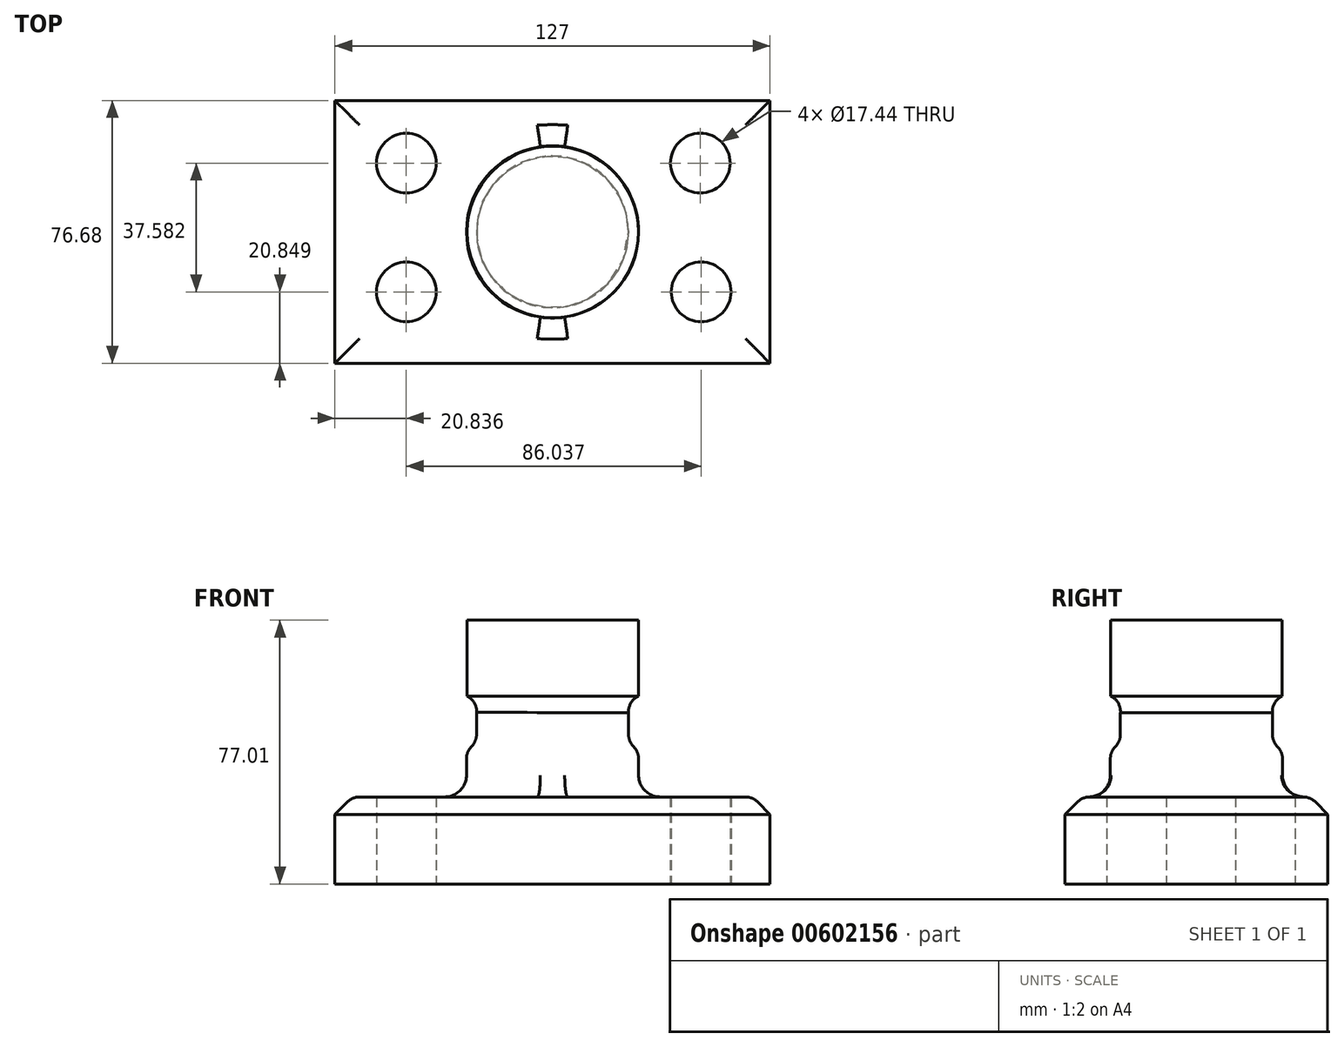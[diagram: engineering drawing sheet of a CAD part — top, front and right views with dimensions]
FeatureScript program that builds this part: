
annotation { "Feature Type Name" : "Feature", "Feature Type Description" : "" }
export const myFeature = defineFeature(function(context is Context, id is Id, definition is map)
    precondition{}
    {
        {
            var Q0;
            Q0=qCreatedBy(makeId("Top.planeOp"),FACE);
            var sketch = newSketch(context, id + "F0", { "sketchPlane" : qUnion([Q0])});
            skLineSegment(sketch, "E0.bottom", {"start": v(63.5, -38.34) * mm, "end": v(-63.5, -38.34) * mm});
            skLineSegment(sketch, "E0.top", {"start": v(63.5, 38.34) * mm, "end": v(-63.5, 38.34) * mm});
            skLineSegment(sketch, "E0.left", {"start": v(63.5, -38.34) * mm, "end": v(63.5, 38.34) * mm});
            skLineSegment(sketch, "E0.right", {"start": v(-63.5, -38.34) * mm, "end": v(-63.5, 38.34) * mm});
            skPoint(sketch, "E0.middle", {"position": v(0, 0) * mm});
            skSolve(sketch);
        }
        {
            var Q0;
            Q0=makeQuery(id+"F0.imprint","IMPRINT",FACE,{"disambiguationData":[TD([[makeQuery(id+"F0.imprint","IMPRINT",EDGE,{"derivedFrom":sQuery(id+"F0.wireOp",EDGE,"E0.bottom")}),-1.0]])]});
            var Q1;
            Q1=sQuery(id+"F0.wireOp",EDGE,"E0.bottom");
            var Q2;
            Q2=sQuery(id+"F0.wireOp",EDGE,"E0.top");
            extrude(context, id + "F1", {"entities" : qUnion([Q0]), "surfaceEntities" : qUnion([Q1, Q2]), "depth" : 25.4 * mm, "offsetDistance" : 25.4 * mm});
        }
        {
            var Q0;
            Q0=makeQuery(id+"F1.opExtrude","CAP_EDGE",EDGE,{"disambiguationData":[OSD([sQuery(id+"F0.wireOp",EDGE,"E0.bottom")])],"isStart":false});
            var Q1;
            Q1=makeQuery(id+"F1.opExtrude","CAP_EDGE",EDGE,{"disambiguationData":[OSD([sQuery(id+"F0.wireOp",EDGE,"E0.right")])],"isStart":false});
            var Q2;
            Q2=makeQuery(id+"F1.opExtrude","CAP_FACE",FACE,{"disambiguationData":[OSD([sQuery(id+"F0.wireOp",EDGE,"E0.bottom"),sQuery(id+"F0.wireOp",EDGE,"E0.top"),sQuery(id+"F0.wireOp",EDGE,"E0.left"),sQuery(id+"F0.wireOp",EDGE,"E0.right")])],"isStart":false});
            chamfer(context, id + "F2", {"entities" : qUnion([Q0, Q1, Q2]), "width" : 5.08 * mm, "tangentPropagation" : true});
        }
        {
            var Q0;
            Q0=qCreatedBy(makeId("Top.planeOp"),FACE);
            var sketch = newSketch(context, id + "F3", { "sketchPlane" : qUnion([Q0])});
            skCircle(sketch, "E1", {"center": v(-42.66, 20.1) * mm, "radius": 8.72 * mm});
            skCircle(sketch, "E2", {"center": v(-42.66, -17.5) * mm, "radius": 8.72 * mm});
            skCircle(sketch, "E3", {"center": v(43.37, -17.5) * mm, "radius": 8.72 * mm});
            skCircle(sketch, "E4", {"center": v(43.14, 20.1) * mm, "radius": 8.72 * mm});
            skSolve(sketch);
        }
        {
            var Q0;
            Q0=makeQuery(id+"F3.imprint","IMPRINT",FACE,{"disambiguationData":[TD([[makeQuery(id+"F3.imprint","IMPRINT",EDGE,{"derivedFrom":sQuery(id+"F3.wireOp",EDGE,"E2")}),1.0]])]});
            var Q1;
            Q1=makeQuery(id+"F3.imprint","IMPRINT",FACE,{"disambiguationData":[TD([[makeQuery(id+"F3.imprint","IMPRINT",EDGE,{"derivedFrom":sQuery(id+"F3.wireOp",EDGE,"E1")}),1.0]])]});
            var Q2;
            Q2=makeQuery(id+"F3.imprint","IMPRINT",FACE,{"disambiguationData":[TD([[makeQuery(id+"F3.imprint","IMPRINT",EDGE,{"derivedFrom":sQuery(id+"F3.wireOp",EDGE,"E4")}),1.0]])]});
            var Q3;
            Q3=makeQuery(id+"F3.imprint","IMPRINT",FACE,{"disambiguationData":[TD([[makeQuery(id+"F3.imprint","IMPRINT",EDGE,{"derivedFrom":sQuery(id+"F3.wireOp",EDGE,"E3")}),1.0]])]});
            extrude(context, id + "F4", {"entities" : qUnion([Q0, Q1, Q2, Q3]), "operationType" : NewBodyOperationType.REMOVE, "depth" : 54.6 * mm, "offsetDistance" : 25.4 * mm});
        }
        {
            var Q0;
            Q0=qCreatedBy(makeId("Top.planeOp"),FACE);
            var sketch = newSketch(context, id + "F5", { "sketchPlane" : qUnion([Q0])});
            skCircle(sketch, "E5", {"center": v(0, 0) * mm, "radius": 25.12 * mm});
            skCircle(sketch, "E6", {"center": v(0, 0) * mm, "radius": 22.18 * mm});
            skSolve(sketch);
        }
        {
            var Q0;
            Q0=makeQuery(id+"F5.imprint","IMPRINT",FACE,{"disambiguationData":[TD([[makeQuery(id+"F5.imprint","IMPRINT",EDGE,{"derivedFrom":sQuery(id+"F5.wireOp",EDGE,"E5")}),1.0]])]});
            extrude(context, id + "F6", {"entities" : qUnion([Q0]), "operationType" : NewBodyOperationType.ADD, "depth" : 41.15 * mm, "offsetDistance" : 25.4 * mm});
        }
        {
            var Q0;
            Q0=makeQuery(id+"F6.boolean.opBoolean","SPLIT",FACE,{"disambiguationData":[TD([makeQuery(id+"F6.opExtrude","SWEPT_FACE",FACE,{"disambiguationData":[OSD([sQuery(id+"F5.wireOp",EDGE,"E6")])]})])],"derivedFrom":makeQuery(id+"F1.opExtrude","CAP_FACE",FACE,{"disambiguationData":[OSD([sQuery(id+"F0.wireOp",EDGE,"E0.bottom"),sQuery(id+"F0.wireOp",EDGE,"E0.top"),sQuery(id+"F0.wireOp",EDGE,"E0.left"),sQuery(id+"F0.wireOp",EDGE,"E0.right")])],"isStart":false})});
            extrude(context, id + "F7", {"entities" : qUnion([Q0]), "operationType" : NewBodyOperationType.ADD, "depth" : 29.46 * mm, "offsetDistance" : 25.4 * mm});
        }
        {
            var Q0;
            Q0=makeQuery(id+"F6.opExtrude","CAP_EDGE",EDGE,{"disambiguationData":[OSD([sQuery(id+"F5.wireOp",EDGE,"E5")])],"isStart":false});
            var Q1;
            Q1=makeQuery(id+"F7.opExtrude","CAP_EDGE",EDGE,{"disambiguationData":[OSD([sQuery(id+"F0.wireOp",EDGE,"E0.bottom"),sQuery(id+"F0.wireOp",EDGE,"E0.top"),sQuery(id+"F0.wireOp",EDGE,"E0.left"),sQuery(id+"F0.wireOp",EDGE,"E0.right"),sQuery(id+"F5.wireOp",EDGE,"E6")])],"isStart":false});
            fillet(context, id + "F8", {"entities" : qUnion([Q0, Q1]), "radius" : 5.08 * mm, "tangentPropagation" : true, "allowEdgeOverflow" : false});
        }
        {
            var Q0;
            {var subQ0=sQuery(id+"F0.wireOp",EDGE,"E0.bottom");Q0=makeQuery(id+"F2.opChamfer","BLEND_EDGE",EDGE,{"blendedFrom":[makeQuery(id+"F1.opExtrude","CAP_EDGE",EDGE,{"disambiguationData":[OSD([subQ0])],"isStart":false}),makeQuery(id+"F1.opExtrude","CAP_FACE",FACE,{"disambiguationData":[OSD([subQ0,sQuery(id+"F0.wireOp",EDGE,"E0.top"),sQuery(id+"F0.wireOp",EDGE,"E0.left"),sQuery(id+"F0.wireOp",EDGE,"E0.right")])],"isStart":false})],"blendedInto":[makeQuery(id+"F1.opExtrude","CAP_FACE",FACE,{"disambiguationData":[OSD([subQ0,sQuery(id+"F0.wireOp",EDGE,"E0.top"),sQuery(id+"F0.wireOp",EDGE,"E0.left"),sQuery(id+"F0.wireOp",EDGE,"E0.right")])],"isStart":false})]});}
            var Q1;
            {var subQ0=sQuery(id+"F0.wireOp",EDGE,"E0.left");Q1=makeQuery(id+"F2.opChamfer","BLEND_EDGE",EDGE,{"blendedFrom":[makeQuery(id+"F1.opExtrude","CAP_EDGE",EDGE,{"disambiguationData":[OSD([subQ0])],"isStart":false}),makeQuery(id+"F1.opExtrude","CAP_FACE",FACE,{"disambiguationData":[OSD([sQuery(id+"F0.wireOp",EDGE,"E0.bottom"),sQuery(id+"F0.wireOp",EDGE,"E0.top"),subQ0,sQuery(id+"F0.wireOp",EDGE,"E0.right")])],"isStart":false})],"blendedInto":[makeQuery(id+"F1.opExtrude","CAP_FACE",FACE,{"disambiguationData":[OSD([sQuery(id+"F0.wireOp",EDGE,"E0.bottom"),sQuery(id+"F0.wireOp",EDGE,"E0.top"),subQ0,sQuery(id+"F0.wireOp",EDGE,"E0.right")])],"isStart":false})]});}
            var Q2;
            {var subQ0=sQuery(id+"F0.wireOp",EDGE,"E0.right");Q2=makeQuery(id+"F2.opChamfer","BLEND_EDGE",EDGE,{"blendedFrom":[makeQuery(id+"F1.opExtrude","CAP_EDGE",EDGE,{"disambiguationData":[OSD([subQ0])],"isStart":false}),makeQuery(id+"F1.opExtrude","CAP_FACE",FACE,{"disambiguationData":[OSD([sQuery(id+"F0.wireOp",EDGE,"E0.bottom"),sQuery(id+"F0.wireOp",EDGE,"E0.top"),sQuery(id+"F0.wireOp",EDGE,"E0.left"),subQ0])],"isStart":false})],"blendedInto":[makeQuery(id+"F1.opExtrude","CAP_FACE",FACE,{"disambiguationData":[OSD([sQuery(id+"F0.wireOp",EDGE,"E0.bottom"),sQuery(id+"F0.wireOp",EDGE,"E0.top"),sQuery(id+"F0.wireOp",EDGE,"E0.left"),subQ0])],"isStart":false})]});}
            var Q3;
            {var subQ0=sQuery(id+"F0.wireOp",EDGE,"E0.top");Q3=makeQuery(id+"F2.opChamfer","BLEND_EDGE",EDGE,{"blendedFrom":[makeQuery(id+"F1.opExtrude","CAP_EDGE",EDGE,{"disambiguationData":[OSD([subQ0])],"isStart":false}),makeQuery(id+"F1.opExtrude","CAP_FACE",FACE,{"disambiguationData":[OSD([sQuery(id+"F0.wireOp",EDGE,"E0.bottom"),subQ0,sQuery(id+"F0.wireOp",EDGE,"E0.left"),sQuery(id+"F0.wireOp",EDGE,"E0.right")])],"isStart":false})],"blendedInto":[makeQuery(id+"F1.opExtrude","CAP_FACE",FACE,{"disambiguationData":[OSD([sQuery(id+"F0.wireOp",EDGE,"E0.bottom"),subQ0,sQuery(id+"F0.wireOp",EDGE,"E0.left"),sQuery(id+"F0.wireOp",EDGE,"E0.right")])],"isStart":false})]});}
            fillet(context, id + "F9", {"entities" : qUnion([Q0, Q1, Q2, Q3]), "radius" : 5.08 * mm, "tangentPropagation" : true, "allowEdgeOverflow" : false});
        }
        {
            var Q0;
            Q0=qCreatedBy(makeId("Front.planeOp"),FACE);
            var sketch = newSketch(context, id + "F10", { "sketchPlane" : qUnion([Q0])});
            skLineSegment(sketch, "E7.bottom", {"start": v(0.07, 54.86) * mm, "end": v(25.06, 54.86) * mm});
            skLineSegment(sketch, "E7.top", {"start": v(0.07, 77) * mm, "end": v(25.06, 77) * mm});
            skLineSegment(sketch, "E7.left", {"start": v(0.07, 54.86) * mm, "end": v(0.07, 77) * mm});
            skLineSegment(sketch, "E7.right", {"start": v(25.06, 54.86) * mm, "end": v(25.06, 77) * mm});
            skSolve(sketch);
        }
        {
            var Q0;
            Q0=makeQuery(id+"F10.imprint","IMPRINT",FACE,{"disambiguationData":[TD([[makeQuery(id+"F10.imprint","IMPRINT",EDGE,{"derivedFrom":sQuery(id+"F10.wireOp",EDGE,"E7.bottom")}),1.0]])]});
            var Q1;
            Q1=sQuery(id+"F10.wireOp",EDGE,"E7.left");
            revolve(context, id + "F11", {"operationType" : NewBodyOperationType.ADD, "entities" : qUnion([Q0]), "axis" : qUnion([Q1]), "revolveType" : RevolveType.FULL});
        }
        {
            var Q0;
            Q0=makeQuery(id+"F8.opFillet","BLEND_FACE",FACE,{"disambiguationData":[OSD([sQuery(id+"F0.wireOp",EDGE,"E0.bottom"),sQuery(id+"F0.wireOp",EDGE,"E0.top"),sQuery(id+"F0.wireOp",EDGE,"E0.left"),sQuery(id+"F0.wireOp",EDGE,"E0.right"),sQuery(id+"F5.wireOp",EDGE,"E6")])]});
            fillet(context, id + "F12", {"entities" : qUnion([Q0]), "radius" : 5.08 * mm, "tangentPropagation" : true, "allowEdgeOverflow" : false});
        }
        {
            var Q0;
            Q0=makeQuery(id+"F6.boolean.opBoolean","INTERSECT",EDGE,{"derivedFrom":[makeQuery(id+"F1.opExtrude","CAP_FACE",FACE,{"disambiguationData":[OSD([sQuery(id+"F0.wireOp",EDGE,"E0.bottom"),sQuery(id+"F0.wireOp",EDGE,"E0.top"),sQuery(id+"F0.wireOp",EDGE,"E0.left"),sQuery(id+"F0.wireOp",EDGE,"E0.right")])],"isStart":false}),makeQuery(id+"F6.opExtrude","SWEPT_FACE",FACE,{"disambiguationData":[OSD([sQuery(id+"F5.wireOp",EDGE,"E5")])]})]});
            fillet(context, id + "F13", {"entities" : qUnion([Q0]), "radius" : 6.35 * mm, "tangentPropagation" : true, "allowEdgeOverflow" : false});
        }
        {
            var Q0;
            Q0=makeQuery(id+"F8.opFillet","BLEND_EDGE",EDGE,{"blendedFrom":[makeQuery(id+"F6.opExtrude","CAP_EDGE",EDGE,{"disambiguationData":[OSD([sQuery(id+"F5.wireOp",EDGE,"E5")])],"isStart":false}),makeQuery(id+"F7.opExtrude","SWEPT_FACE",FACE,{"disambiguationData":[OSD([sQuery(id+"F0.wireOp",EDGE,"E0.bottom"),sQuery(id+"F0.wireOp",EDGE,"E0.top"),sQuery(id+"F0.wireOp",EDGE,"E0.left"),sQuery(id+"F0.wireOp",EDGE,"E0.right"),sQuery(id+"F5.wireOp",EDGE,"E6")])]})],"blendedInto":[makeQuery(id+"F7.opExtrude","SWEPT_FACE",FACE,{"disambiguationData":[OSD([sQuery(id+"F0.wireOp",EDGE,"E0.bottom"),sQuery(id+"F0.wireOp",EDGE,"E0.top"),sQuery(id+"F0.wireOp",EDGE,"E0.left"),sQuery(id+"F0.wireOp",EDGE,"E0.right"),sQuery(id+"F5.wireOp",EDGE,"E6")])]})]});
            fillet(context, id + "F14", {"entities" : qUnion([Q0]), "radius" : 5.08 * mm, "tangentPropagation" : true, "allowEdgeOverflow" : false});
        }
    });
